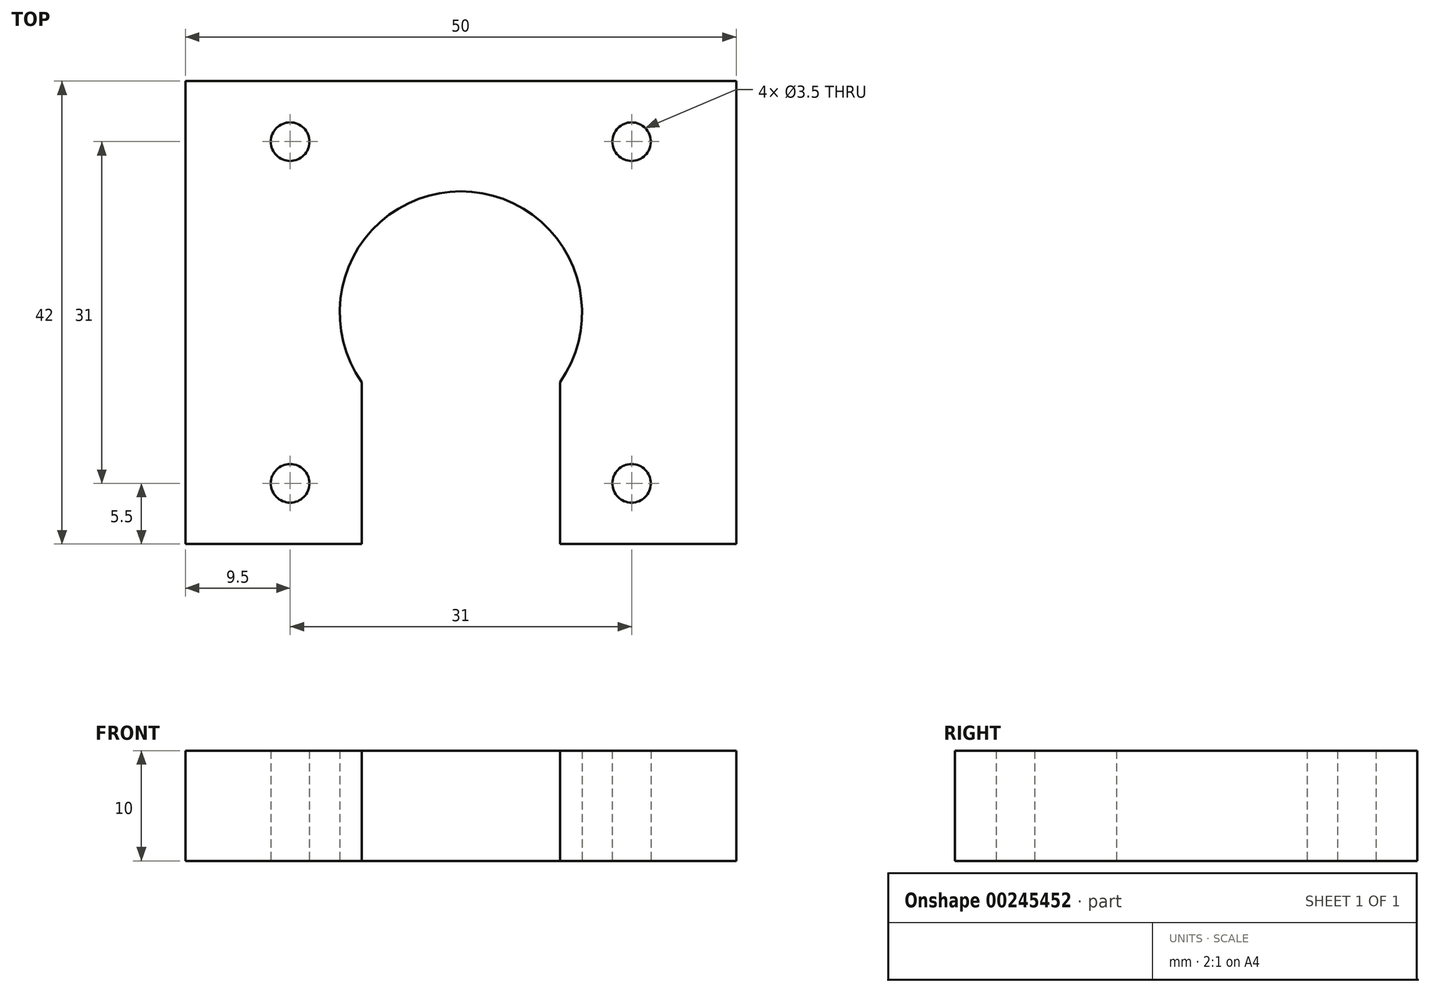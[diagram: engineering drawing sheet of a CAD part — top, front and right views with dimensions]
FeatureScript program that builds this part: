
annotation { "Feature Type Name" : "Feature", "Feature Type Description" : "" }
export const myFeature = defineFeature(function(context is Context, id is Id, definition is map)
    precondition{}
    {
        {
            var Q0;
            Q0=qCreatedBy(makeId("Top.planeOp"),FACE);
            var sketch = newSketch(context, id + "F0", { "sketchPlane" : qUnion([Q0])});
            skLineSegment(sketch, "E0", {"start": v(-25, 21) * mm, "end": v(-25, -21) * mm});
            skLineSegment(sketch, "E1", {"start": v(-25, -21) * mm, "end": v(-9, -21) * mm});
            skLineSegment(sketch, "E2", {"start": v(-9, -21) * mm, "end": v(-9, -6.32) * mm});
            skLineSegment(sketch, "E3", {"start": v(-25, 21) * mm, "end": v(25, 21) * mm});
            skLineSegment(sketch, "E4", {"start": v(25, 21) * mm, "end": v(25, -21) * mm});
            skLineSegment(sketch, "E5", {"start": v(25, -21) * mm, "end": v(9, -21) * mm});
            skLineSegment(sketch, "E6", {"start": v(9, -21) * mm, "end": v(9, -6.32) * mm});
            skArc(sketch, "E7", {"start": v(9, -6.32) * mm, "mid": v(0, 11) * mm, "end": v(-9, -6.32) * mm});
            skCircle(sketch, "E8", {"center": v(-15.5, 15.5) * mm, "radius": 1.75 * mm});
            skCircle(sketch, "E9", {"center": v(-15.5, -15.5) * mm, "radius": 1.75 * mm});
            skCircle(sketch, "E10", {"center": v(15.5, -15.5) * mm, "radius": 1.75 * mm});
            skCircle(sketch, "E11", {"center": v(15.5, 15.5) * mm, "radius": 1.75 * mm});
            skSolve(sketch);
        }
        {
            var Q0;
            Q0=makeQuery(id+"F0.imprint","IMPRINT",FACE,{"disambiguationData":[TD([[makeQuery(id+"F0.imprint","IMPRINT",EDGE,{"derivedFrom":sQuery(id+"F0.wireOp",EDGE,"E0")}),1.0]])]});
            extrude(context, id + "F1", {"entities" : qUnion([Q0]), "depth" : 10 * mm});
        }
    });
